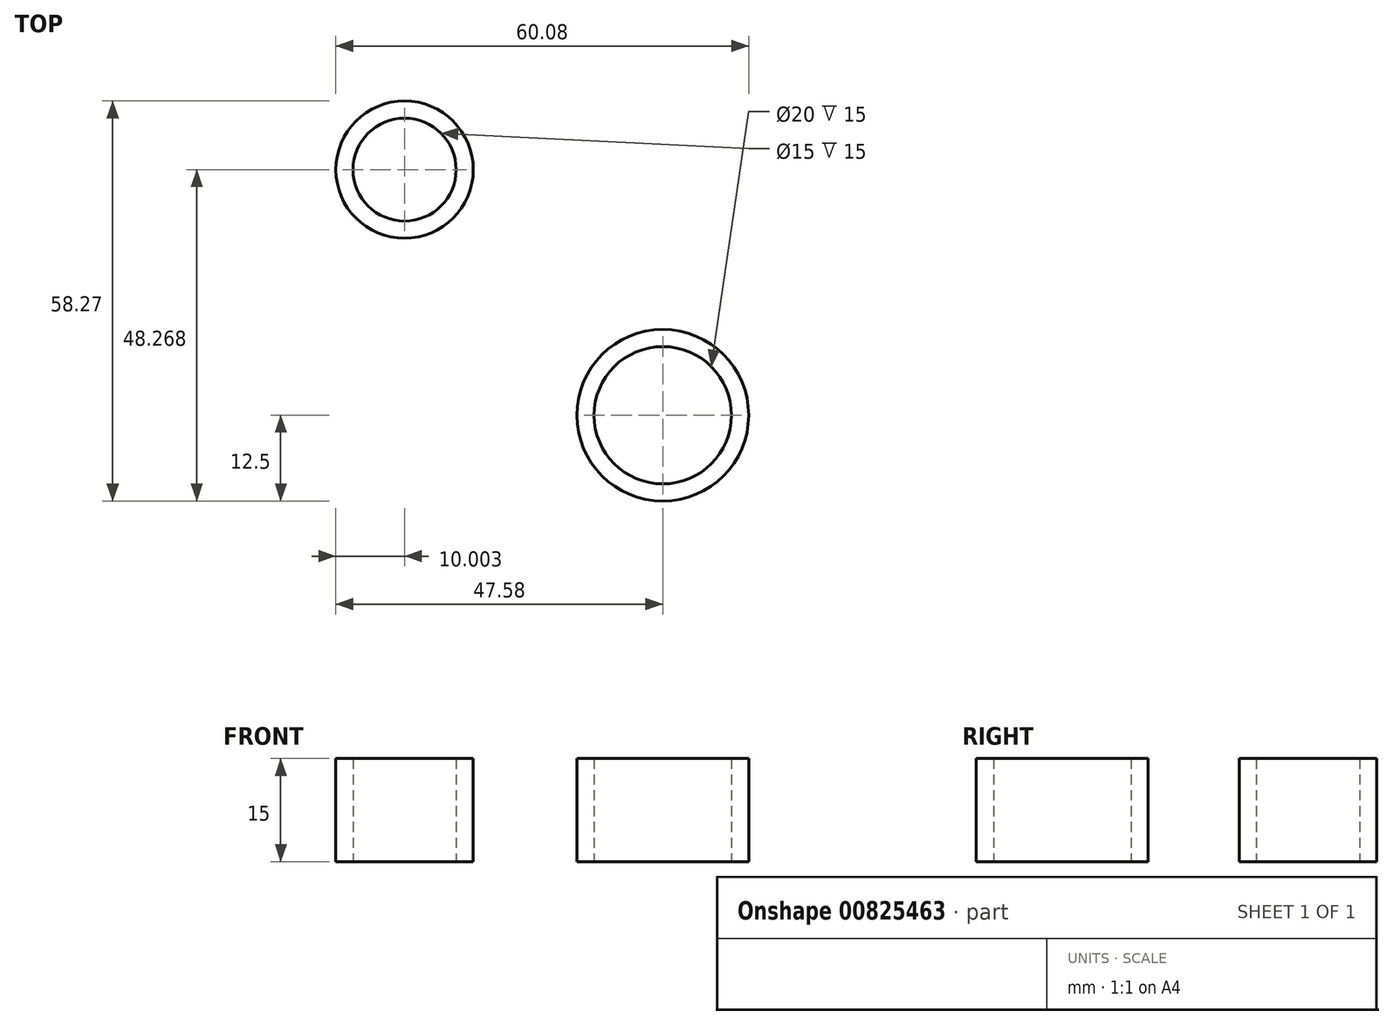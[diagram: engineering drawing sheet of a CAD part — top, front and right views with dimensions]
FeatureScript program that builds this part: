
annotation { "Feature Type Name" : "Feature", "Feature Type Description" : "" }
export const myFeature = defineFeature(function(context is Context, id is Id, definition is map)
    precondition{}
    {
        {
            var Q0;
            Q0=qCreatedBy(makeId("Top.planeOp"),FACE);
            var sketch = newSketch(context, id + "F0", { "sketchPlane" : qUnion([Q0])});
            skCircle(sketch, "E0", {"center": v(0, 0) * mm, "radius": 12.5 * mm});
            skCircle(sketch, "E1", {"center": v(0, 0) * mm, "radius": 10 * mm});
            skCircle(sketch, "E2", {"center": v(-37.58, 35.77) * mm, "radius": 10 * mm});
            skCircle(sketch, "E3", {"center": v(-37.58, 35.77) * mm, "radius": 7.5 * mm});
            skSolve(sketch);
        }
        {
            var Q0;
            Q0 = qSketchRegion(id + "F0", true);
            extrude(context, id + "F1", {"entities" : qUnion([Q0]), "depth" : 15 * mm, "offsetDistance" : 25 * mm});
        }
    });
